# Revit family: Atdec-Wallmount-AD-WT50-Landscape-
name_source: partatom
category: Generic Models
revit_build: Autodesk Revit 2016 (Build: 20150220_1215(x64)
units: mm (PartAtom-declared; Revit-internal decimal feet)

## family parameters
Can host rebar = No
Cut with Voids When Loaded = No
Host = Face
Part Type = Normal
Room Calculation Point = No
Round Connector Dimension = Use Diameter
Shared = No

## types (2) — shared parameters
Assembly Code = E1010800
Colour Options = Black
Default Elevation = 1219 mm
Flat screen maximum supported weight = 50kg (110lb)
Manufacturer = Atdec
Material = Steel
Maximum distance from wall (mm) = 56mm (2.20")
Minimum distance from wall (mm) = 56mm (2.20")
Pan Adjustment = -
Product Family = Wall Mount Rail
Product Information Link = https://www.atdec.com.au
Range of Motion = Tilt
Security feature = -
Single units per master pack = 8
Tilt Adjustment = 10° of downward and 5° of upward tilt
UPC Code = 881493019195
URL = www.atdec.com.au
Universal Height (mm) = From 100 to 400
Warranty = 10 years

## per-type parameters (varying)
| type | Description | Master Carton Dimensions | Plate Width | Single Unit Dimensions | Universal Width (mm) | VESA mounting hole pattern, mm | Weight, Single Unit | Weight, master carton |
| AD-WT-5040 | Tilting angle wall mount VESA up to 400x400 | 485mm (19.1") Length, 283mm (11.1") Width, 330mm (13") Height | 448 mm  [stored 1.46982 ft] | 470mm (18.5") Length, 155mm (6.1") Width, 65mm (2.6") Height | From 100 to 400 | 100x100, 100x200, 200x100, 200x200, 200x300, 200x400, 300x200, 300x300, 400x200, 400x300, 400x400 | 2.16 (4.76lb) | 18.26kg (40.26lb) |
| AD-WT-5060 | Tilting angle wall mount VESA up to 600x400 | 690mm (27.2") Length, 283mm (11.1") Width, 330mm (13") Height | 653 mm  [stored 2.14239 ft] | 675mm (26.6") Length, 155mm (6.1") Width, 65mm (2.6") Height | From 100 to 600 | 100x100, 100x200, 200x100, 200x200, 200x300, 200x400, 300x200, 300x300, 400x200, 400x300, 400x400, 600x200, 600x400 | 2.64 (5.82lb) | 21.94kg (48.37lb) |

note: column(s) folded — value = type name in every type: Model

note: [stored X ft] marks values corroborated as IEEE doubles in the binary element streams (Revit-internal decimal feet)

## geometry (parser evidence)
native form markers: Sweep x3
no freeform markers — native parametric forms only
